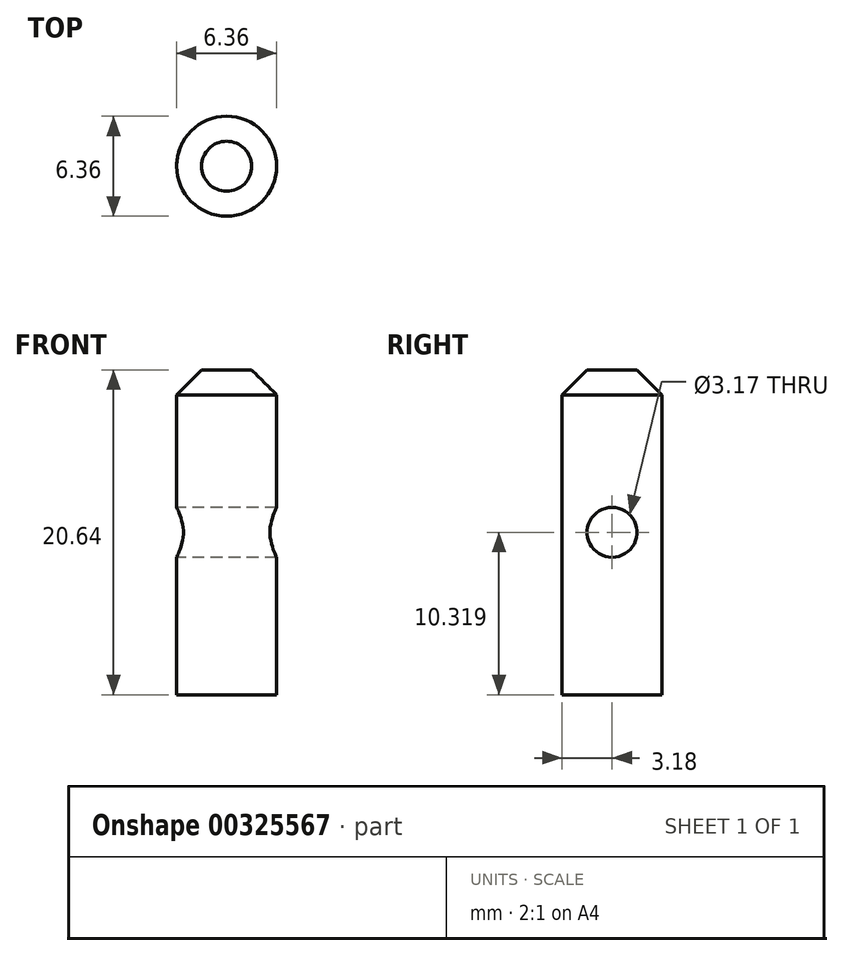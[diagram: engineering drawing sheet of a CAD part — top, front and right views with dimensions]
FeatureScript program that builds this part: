
annotation { "Feature Type Name" : "Feature", "Feature Type Description" : "" }
export const myFeature = defineFeature(function(context is Context, id is Id, definition is map)
    precondition{}
    {
        {
            var Q0;
            Q0=qCreatedBy(makeId("Top.planeOp"),FACE);
            var sketch = newSketch(context, id + "F0", { "sketchPlane" : qUnion([Q0])});
            skCircle(sketch, "E0", {"center": v(0, 0) * mm, "radius": 3.18 * mm});
            skSolve(sketch);
        }
        {
            var Q0;
            Q0=makeQuery(id+"F0.imprint","IMPRINT",FACE,{"disambiguationData":[TD([[makeQuery(id+"F0.imprint","IMPRINT",EDGE,{"derivedFrom":sQuery(id+"F0.wireOp",EDGE,"E0")}),1.0]])]});
            extrude(context, id + "F1", {"entities" : qUnion([Q0]), "depth" : 20.64 * mm});
        }
        {
            var Q0;
            Q0=makeQuery(id+"F1.opExtrude","CAP_EDGE",EDGE,{"disambiguationData":[OSD([sQuery(id+"F0.wireOp",EDGE,"E0")])],"isStart":false});
            chamfer(context, id + "F2", {"entities" : qUnion([Q0]), "width" : 1.59 * mm, "tangentPropagation" : true});
        }
        {
            var Q0;
            Q0=qCreatedBy(makeId("Right.planeOp"),FACE);
            var sketch = newSketch(context, id + "F3", { "sketchPlane" : qUnion([Q0])});
            skCircle(sketch, "E1", {"center": v(0, 10.32) * mm, "radius": 1.59 * mm});
            skSolve(sketch);
        }
        {
            var Q0;
            Q0 = qSketchRegion(id + "F3", true);
            extrude(context, id + "F4", {"entities" : qUnion([Q0]), "operationType" : NewBodyOperationType.REMOVE, "endBound" : BoundingType.SYMMETRIC, "depth" : 25.4 * mm});
        }
    });
